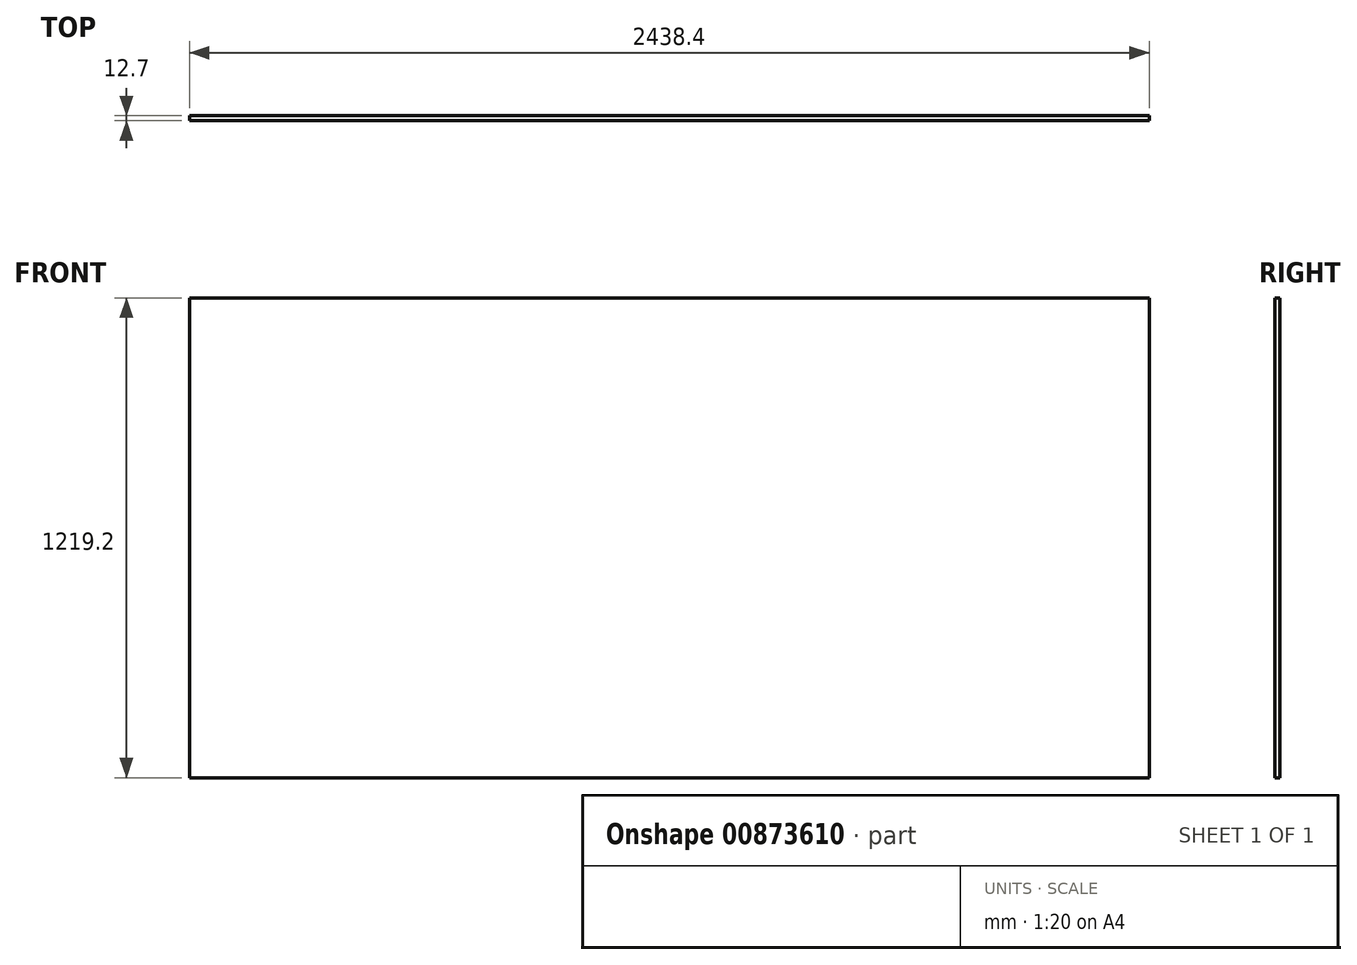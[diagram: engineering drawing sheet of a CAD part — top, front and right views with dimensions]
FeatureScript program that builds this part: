
annotation { "Feature Type Name" : "Feature", "Feature Type Description" : "" }
export const myFeature = defineFeature(function(context is Context, id is Id, definition is map)
    precondition{}
    {
        {
            var Q0;
            Q0=qCreatedBy(makeId("Front.planeOp"),FACE);
            var sketch = newSketch(context, id + "F0", { "sketchPlane" : qUnion([Q0])});
            skLineSegment(sketch, "E0.bottom", {"start": v(0, 0) * mm, "end": v(2438.4, 0) * mm});
            skLineSegment(sketch, "E0.top", {"start": v(0, 1219.2) * mm, "end": v(2438.4, 1219.2) * mm});
            skLineSegment(sketch, "E0.left", {"start": v(0, 0) * mm, "end": v(0, 1219.2) * mm});
            skLineSegment(sketch, "E0.right", {"start": v(2438.4, 0) * mm, "end": v(2438.4, 1219.2) * mm});
            skSolve(sketch);
        }
        {
            var Q0;
            Q0=makeQuery(id+"F0.imprint","IMPRINT",FACE,{"disambiguationData":[TD([[makeQuery(id+"F0.imprint","IMPRINT",EDGE,{"derivedFrom":sQuery(id+"F0.wireOp",EDGE,"E0.bottom")}),1.0]])]});
            extrude(context, id + "F1", {"entities" : qUnion([Q0]), "depth" : 12.7 * mm, "offsetDistance" : 25.4 * mm});
        }
    });
